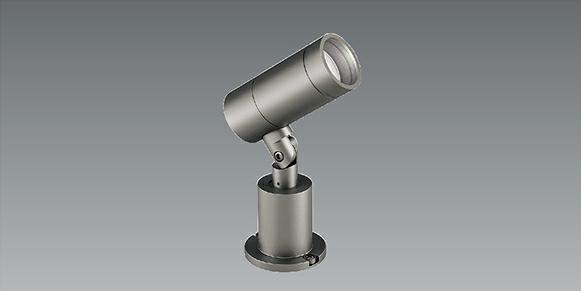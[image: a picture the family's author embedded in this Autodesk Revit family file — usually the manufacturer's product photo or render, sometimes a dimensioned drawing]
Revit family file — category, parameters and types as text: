
# Revit family: ERS6366HC_RAD843F
name_source: partatom
category: 照明器具
units: mm (PartAtom-declared; Revit-internal decimal feet)

## family parameters
OmniClass タイトル = Spots and Tracklight Specialties
OmniClass 番号 = 23.80.70.11.14.21
パーツ タイプ = 標準
ロード時にボイドで切り取り = はい
丸型コネクタ寸法 = 直径を使用
作業面ベース = いいえ
光源 = いいえ
共有 = いいえ
常に垂直 = いいえ
注釈の向きを維持 = いいえ
部屋計算ポイント = はい

## types (1)
- ERS6366HC_RAD843F
    BLCJ仕様バージョン = 2
    Clearance Back = 0  [stored 0 ft]
    Clearance Bottom = 0  [stored 0 ft]
    Clearance Front = 0  [stored 0 ft]
    Clearance Left = 0  [stored 0 ft]
    Clearance Right = 0  [stored 0 ft]
    Clearance Top = 0  [stored 0 ft]
    Depth = 0  [stored 0 ft]
    FamilyVersion = v2.0
    Height = 93  [stored 0.305118 ft]
    IfcExportAs = IfcLightFixtureType
    IfcExportType = DIRECTIONSOURCE
    OmniClassCode = 23.80.70.11.14.21
    URL = https://data2.endo-lighting.co.jp
    Width = 0  [stored 0 ft]
    イメージ(タイプ) = ERS6366HC_RAD843F-K.jpg
    サービススペース表示 = いいえ
    シンボル表示 = はい
    データ作成年月 = 2025.04
    モデル = ERS6366HC_RAD843F
    ランプ = LED
    ランプ_全光束 = 0 lm
    ランプ_定格消費効率(lm/W) = 0
    ランプ_定格消費電力 = 0 W
    ランプ_本数 = 0
    ランプ_電流 = 0 A
    ランプの種類 = LED
    価格 = 17500 $
    分類グループ = 電気
    分類コード = 40305100000000
    周波数 = 0 Hz
    呼称 = 投光器・屋外スポット
    固有エネルギー消費効率(lm/W) = 62.6
    埋込深さ = 0
    埋込穴寸法 = 0
    安定器_二次電圧 = 0 V
    安定器_入力電力 = 0 W
    安定器_入力電流 = 0 A
    安定器_定格電圧 = 0 V
    定格光束 = 370 lm
    定格入力容量 = 0 VA
    定格入力電圧 = 0 V
    定格入力電流 = 0 A
    定格消費電力 = 6 W
    平均演色評価数(Ra) = 83
    既定の高さ = 0  [stored 0 ft]
    材質_カバー = <カテゴリ別>
    材質_ルーバー = <カテゴリ別>
    材質_反射板 = <カテゴリ別>
    材質_本体 = <カテゴリ別>
    極数 = 1
    用途 = E_一般照明
    皮相負荷 = 0 VA
    直径 = 40  [stored 0.131234 ft]
    相 = 1
    積算_科目 = 1 電灯設備
    積算_科目2 = [1_1]照明
    製品リリース年月 = 2024.04
    製品質量 = 0.30 kg
    製造元 = 株式会社遠藤照明
    説明 = アウトドア ミニスポットライト
    負荷分類 = 8_照明
    質量 = 0.00 kg
    運転質量 = 0.00 kg
    配光角 = 0
    電源種別_記号 = AC

note: [stored X ft] marks values corroborated as IEEE doubles in the binary element streams (Revit-internal decimal feet)
